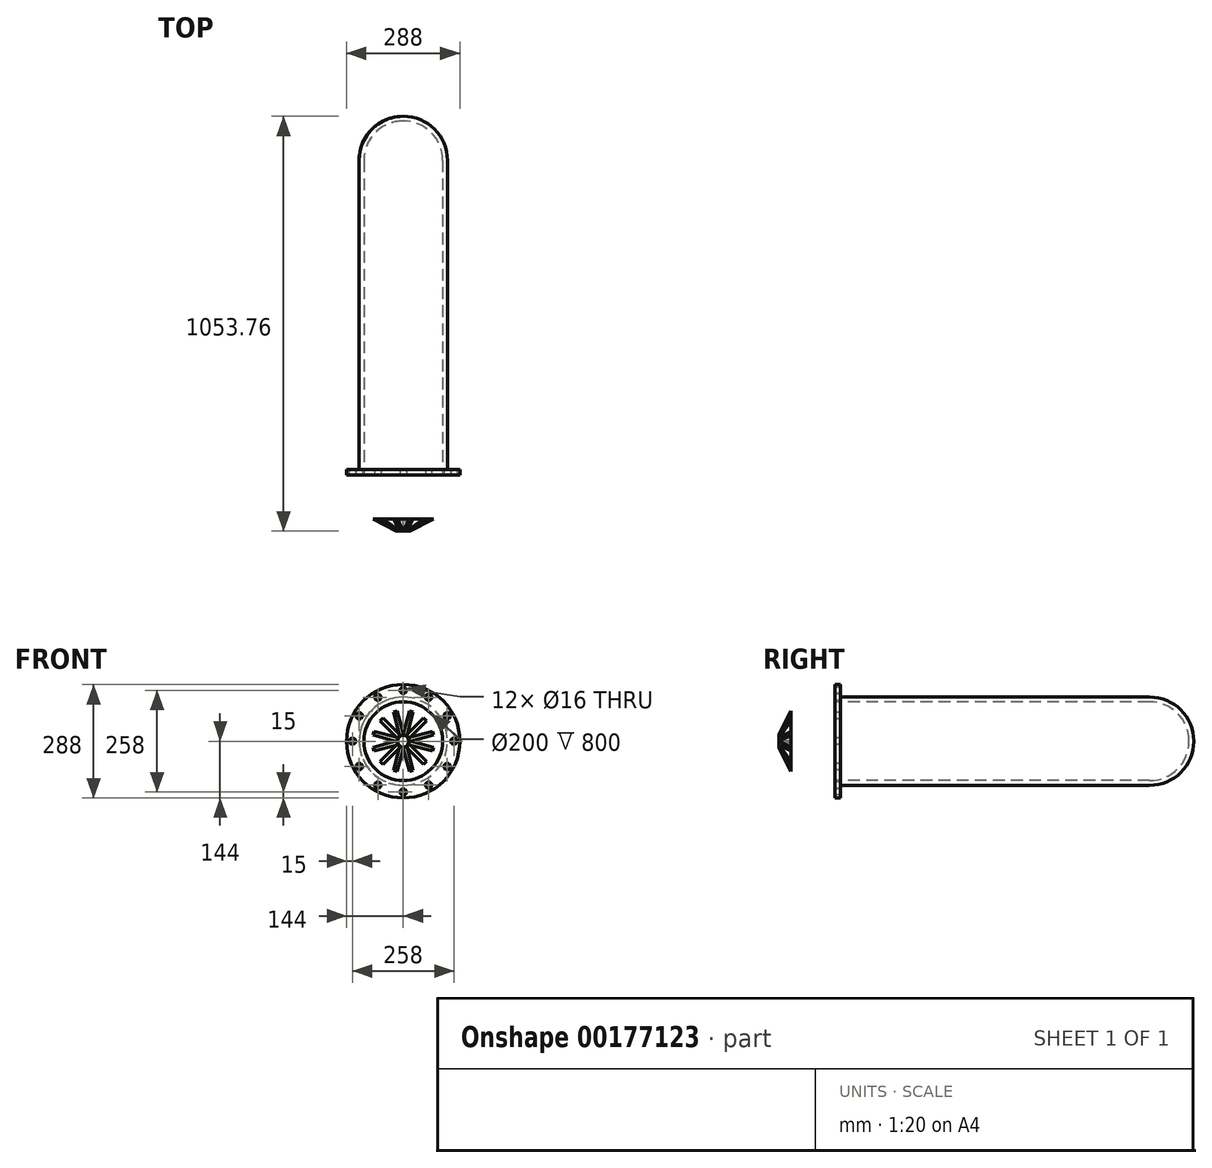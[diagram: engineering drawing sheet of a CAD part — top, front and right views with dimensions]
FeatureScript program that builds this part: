
annotation { "Feature Type Name" : "Feature", "Feature Type Description" : "" }
export const myFeature = defineFeature(function(context is Context, id is Id, definition is map)
    precondition{}
    {
        {
            var Q0;
            Q0=qCreatedBy(makeId("Top.planeOp"),FACE);
            var sketch = newSketch(context, id + "F0", { "sketchPlane" : qUnion([Q0])});
            skLineSegment(sketch, "E0", {"start": v(-144, 0) * mm, "end": v(-100, 0) * mm});
            skLineSegment(sketch, "E1", {"start": v(-100, 0) * mm, "end": v(-100, 800) * mm});
            skLineSegment(sketch, "E2", {"start": v(-144, 0) * mm, "end": v(-144, 14) * mm});
            skLineSegment(sketch, "E3", {"start": v(0, 912) * mm, "end": v(0, 900) * mm});
            skLineSegment(sketch, "E4", {"start": v(0, 0) * mm, "end": v(0, 900) * mm, "construction": true});
            skLineSegment(sketch, "E5", {"start": v(-144, 14) * mm, "end": v(-112, 14) * mm});
            skLineSegment(sketch, "E6", {"start": v(-112, 14) * mm, "end": v(-112, 800) * mm});
            skArc(sketch, "E7", {"start": v(0, 900) * mm, "mid": v(-70.71, 870.71) * mm, "end": v(-100, 800) * mm});
            skArc(sketch, "E8", {"start": v(0, 912) * mm, "mid": v(-79.2, 879.2) * mm, "end": v(-112, 800) * mm});
            skLineSegment(sketch, "E9", {"start": v(-112, 800) * mm, "end": v(0, 800) * mm, "construction": true});
            skSolve(sketch);
        }
        {
            var Q0;
            Q0 = qSketchRegion(id + "F0", true);
            var Q1;
            Q1=sQuery(id+"F0.wireOp",EDGE,"E4");
            revolve(context, id + "F1", {"entities" : qUnion([Q0]), "axis" : qUnion([Q1]), "revolveType" : RevolveType.FULL});
        }
        {
            var Q0;
            Q0=makeQuery(id+"F1.opRevolve","SWEPT_FACE",FACE,{"disambiguationData":[OSD([sQuery(id+"F0.wireOp",EDGE,"E0")])]});
            var sketch = newSketch(context, id + "F2", { "sketchPlane" : qUnion([Q0])});
            skCircle(sketch, "E10", {"center": v(0, 129) * mm, "radius": 8 * mm});
            skSolve(sketch);
        }
        {
            var Q0;
            Q0=makeQuery(id+"F2.imprint","IMPRINT",FACE,{"disambiguationData":[TD([[makeQuery(id+"F2.imprint","IMPRINT",EDGE,{"derivedFrom":sQuery(id+"F2.wireOp",EDGE,"E10")}),1.0]])]});
            extrude(context, id + "F3", {"entities" : qUnion([Q0]), "oppositeDirection" : true, "depth" : 20 * mm});
        }
        {
            var Q0;
            Q0=makeQuery(id+"F3.opExtrude","SWEPT_BODY",BODY,{"disambiguationData":[OSD([sQuery(id+"F2.wireOp",EDGE,"E10")])]});
            var Q1;
            Q1=makeQuery(id+"F1.opRevolve","SWEPT_EDGE",EDGE,{"disambiguationData":[OSD([sQuery(id+"F0.wireOp",EDGE,"E0"),sQuery(id+"F0.wireOp",EDGE,"E2")])]});
            circularPattern(context, id + "F4", {"entities" : qUnion([Q0]), "axis" : qUnion([Q1]), "angle" : 30 * degree, "instanceCount" : 12});
        }
        {
            var Q0;
            Q0=makeQuery(id+"F3.opExtrude","SWEPT_BODY",BODY,{"disambiguationData":[OSD([sQuery(id+"F2.wireOp",EDGE,"E10")])]});
            var Q1;
            Q1=makeQuery(id+"F4.opPattern","COPY",BODY,{"derivedFrom":makeQuery(id+"F3.opExtrude","SWEPT_BODY",BODY,{"disambiguationData":[OSD([sQuery(id+"F2.wireOp",EDGE,"E10")])]}),"instanceName":"1"});
            var Q2;
            Q2=makeQuery(id+"F4.opPattern","COPY",BODY,{"derivedFrom":makeQuery(id+"F3.opExtrude","SWEPT_BODY",BODY,{"disambiguationData":[OSD([sQuery(id+"F2.wireOp",EDGE,"E10")])]}),"instanceName":"4"});
            var Q3;
            Q3=makeQuery(id+"F4.opPattern","COPY",BODY,{"derivedFrom":makeQuery(id+"F3.opExtrude","SWEPT_BODY",BODY,{"disambiguationData":[OSD([sQuery(id+"F2.wireOp",EDGE,"E10")])]}),"instanceName":"3"});
            var Q4;
            Q4=makeQuery(id+"F4.opPattern","COPY",BODY,{"derivedFrom":makeQuery(id+"F3.opExtrude","SWEPT_BODY",BODY,{"disambiguationData":[OSD([sQuery(id+"F2.wireOp",EDGE,"E10")])]}),"instanceName":"2"});
            var Q5;
            Q5=makeQuery(id+"F4.opPattern","COPY",BODY,{"derivedFrom":makeQuery(id+"F3.opExtrude","SWEPT_BODY",BODY,{"disambiguationData":[OSD([sQuery(id+"F2.wireOp",EDGE,"E10")])]}),"instanceName":"9"});
            var Q6;
            Q6=makeQuery(id+"F4.opPattern","COPY",BODY,{"derivedFrom":makeQuery(id+"F3.opExtrude","SWEPT_BODY",BODY,{"disambiguationData":[OSD([sQuery(id+"F2.wireOp",EDGE,"E10")])]}),"instanceName":"10"});
            var Q7;
            Q7=makeQuery(id+"F4.opPattern","COPY",BODY,{"derivedFrom":makeQuery(id+"F3.opExtrude","SWEPT_BODY",BODY,{"disambiguationData":[OSD([sQuery(id+"F2.wireOp",EDGE,"E10")])]}),"instanceName":"11"});
            var Q8;
            Q8=makeQuery(id+"F4.opPattern","COPY",BODY,{"derivedFrom":makeQuery(id+"F3.opExtrude","SWEPT_BODY",BODY,{"disambiguationData":[OSD([sQuery(id+"F2.wireOp",EDGE,"E10")])]}),"instanceName":"8"});
            var Q9;
            Q9=makeQuery(id+"F4.opPattern","COPY",BODY,{"derivedFrom":makeQuery(id+"F3.opExtrude","SWEPT_BODY",BODY,{"disambiguationData":[OSD([sQuery(id+"F2.wireOp",EDGE,"E10")])]}),"instanceName":"7"});
            var Q10;
            Q10=makeQuery(id+"F4.opPattern","COPY",BODY,{"derivedFrom":makeQuery(id+"F3.opExtrude","SWEPT_BODY",BODY,{"disambiguationData":[OSD([sQuery(id+"F2.wireOp",EDGE,"E10")])]}),"instanceName":"6"});
            var Q11;
            Q11=makeQuery(id+"F4.opPattern","COPY",BODY,{"derivedFrom":makeQuery(id+"F3.opExtrude","SWEPT_BODY",BODY,{"disambiguationData":[OSD([sQuery(id+"F2.wireOp",EDGE,"E10")])]}),"instanceName":"5"});
            var Q12;
            Q12=makeQuery(id+"F1.opRevolve","SWEPT_BODY",BODY,{"disambiguationData":[OSD([sQuery(id+"F0.wireOp",EDGE,"E0"),sQuery(id+"F0.wireOp",EDGE,"E1"),sQuery(id+"F0.wireOp",EDGE,"E2"),sQuery(id+"F0.wireOp",EDGE,"E3"),sQuery(id+"F0.wireOp",EDGE,"E5"),sQuery(id+"F0.wireOp",EDGE,"E6"),sQuery(id+"F0.wireOp",EDGE,"E7"),sQuery(id+"F0.wireOp",EDGE,"E8")])]});
            booleanBodies(context, id + "F5", {"operationType" : BooleanOperationType.SUBTRACTION, "tools" : qUnion([Q0, Q1, Q2, Q3, Q4, Q5, Q6, Q7, Q8, Q9, Q10, Q11]), "targets" : qUnion([Q12])});
        }
        {
            var Q0;
            Q0=sQuery(id+"F0.wireOp",EDGE,"E4");
            cPlane(context, id + "F6", {"entities" : qUnion([Q0]), "cplaneType" : CPlaneType.LINE_ANGLE, "offset" : 25 * mm, "angle" : 45 * degree, "width" : 150 * mm, "height" : 150 * mm});
        }
        {
            var Q0;
            Q0=qCreatedBy(id+"F6.planeOp",FACE);
            var sketch = newSketch(context, id + "F7", { "sketchPlane" : qUnion([Q0])});
            skLineSegment(sketch, "E11", {"start": v(-111, 78) * mm, "end": v(-143, 14) * mm});
            skLineSegment(sketch, "E12", {"start": v(-143, 14) * mm, "end": v(-111, 14) * mm});
            skLineSegment(sketch, "E13", {"start": v(-111, 14) * mm, "end": v(-111, 78) * mm});
            skSolve(sketch);
        }
        {
            var Q0;
            Q0=makeQuery(id+"F7.imprint","IMPRINT",FACE,{"disambiguationData":[TD([[makeQuery(id+"F7.imprint","IMPRINT",EDGE,{"derivedFrom":sQuery(id+"F7.wireOp",EDGE,"E11")}),1.0]])]});
            extrude(context, id + "F8", {"entities" : qUnion([Q0]), "endBound" : BoundingType.SYMMETRIC, "depth" : 10 * mm});
        }
        {
            var Q0;
            Q0=makeQuery(id+"F8.opExtrude","SWEPT_BODY",BODY,{"disambiguationData":[OSD([sQuery(id+"F7.wireOp",EDGE,"E11"),sQuery(id+"F7.wireOp",EDGE,"E12"),sQuery(id+"F7.wireOp",EDGE,"E13")])]});
            var Q1;
            Q1=makeQuery(id+"F1.opRevolve","SWEPT_EDGE",EDGE,{"disambiguationData":[OSD([sQuery(id+"F0.wireOp",EDGE,"E2"),sQuery(id+"F0.wireOp",EDGE,"E5")])]});
            circularPattern(context, id + "F9", {"entities" : qUnion([Q0]), "axis" : qUnion([Q1]), "angle" : 30 * degree, "instanceCount" : 12});
        }
        {
            var Q0;
            Q0=makeQuery(id+"F1.opRevolve","SWEPT_FACE",FACE,{"disambiguationData":[OSD([sQuery(id+"F0.wireOp",EDGE,"E6")])]});
            fillet(context, id + "F10", {"entities" : qUnion([Q0]), "radius" : 2 * mm, "tangentPropagation" : true, "allowEdgeOverflow" : false});
        }
        {
            var Q0;
            Q0=makeQuery(id+"F9.opPattern","COPY",EDGE,{"derivedFrom":makeQuery(id+"F8.opExtrude","CAP_EDGE",EDGE,{"disambiguationData":[OSD([sQuery(id+"F7.wireOp",EDGE,"E12")])],"isStart":false}),"instanceName":"3"});
            var Q1;
            Q1=makeQuery(id+"F9.opPattern","COPY",EDGE,{"derivedFrom":makeQuery(id+"F8.opExtrude","SWEPT_EDGE",EDGE,{"disambiguationData":[OSD([sQuery(id+"F7.wireOp",EDGE,"E11"),sQuery(id+"F7.wireOp",EDGE,"E12")])]}),"instanceName":"3"});
            var Q2;
            Q2=makeQuery(id+"F9.opPattern","COPY",EDGE,{"derivedFrom":makeQuery(id+"F8.opExtrude","CAP_EDGE",EDGE,{"disambiguationData":[OSD([sQuery(id+"F7.wireOp",EDGE,"E12")])],"isStart":true}),"instanceName":"3"});
            var Q3;
            Q3=makeQuery(id+"F9.opPattern","COPY",EDGE,{"derivedFrom":makeQuery(id+"F8.opExtrude","CAP_EDGE",EDGE,{"disambiguationData":[OSD([sQuery(id+"F7.wireOp",EDGE,"E12")])],"isStart":false}),"instanceName":"4"});
            var Q4;
            Q4=makeQuery(id+"F9.opPattern","COPY",EDGE,{"derivedFrom":makeQuery(id+"F8.opExtrude","SWEPT_EDGE",EDGE,{"disambiguationData":[OSD([sQuery(id+"F7.wireOp",EDGE,"E11"),sQuery(id+"F7.wireOp",EDGE,"E12")])]}),"instanceName":"4"});
            var Q5;
            Q5=makeQuery(id+"F9.opPattern","COPY",EDGE,{"derivedFrom":makeQuery(id+"F8.opExtrude","CAP_EDGE",EDGE,{"disambiguationData":[OSD([sQuery(id+"F7.wireOp",EDGE,"E12")])],"isStart":true}),"instanceName":"4"});
            var Q6;
            Q6=makeQuery(id+"F9.opPattern","COPY",EDGE,{"derivedFrom":makeQuery(id+"F8.opExtrude","CAP_EDGE",EDGE,{"disambiguationData":[OSD([sQuery(id+"F7.wireOp",EDGE,"E12")])],"isStart":false}),"instanceName":"5"});
            var Q7;
            Q7=makeQuery(id+"F9.opPattern","COPY",EDGE,{"derivedFrom":makeQuery(id+"F8.opExtrude","SWEPT_EDGE",EDGE,{"disambiguationData":[OSD([sQuery(id+"F7.wireOp",EDGE,"E11"),sQuery(id+"F7.wireOp",EDGE,"E12")])]}),"instanceName":"5"});
            var Q8;
            Q8=makeQuery(id+"F9.opPattern","COPY",EDGE,{"derivedFrom":makeQuery(id+"F8.opExtrude","CAP_EDGE",EDGE,{"disambiguationData":[OSD([sQuery(id+"F7.wireOp",EDGE,"E12")])],"isStart":true}),"instanceName":"5"});
            var Q9;
            Q9=makeQuery(id+"F9.opPattern","COPY",EDGE,{"derivedFrom":makeQuery(id+"F8.opExtrude","CAP_EDGE",EDGE,{"disambiguationData":[OSD([sQuery(id+"F7.wireOp",EDGE,"E12")])],"isStart":false}),"instanceName":"6"});
            var Q10;
            Q10=makeQuery(id+"F9.opPattern","COPY",EDGE,{"derivedFrom":makeQuery(id+"F8.opExtrude","SWEPT_EDGE",EDGE,{"disambiguationData":[OSD([sQuery(id+"F7.wireOp",EDGE,"E11"),sQuery(id+"F7.wireOp",EDGE,"E12")])]}),"instanceName":"6"});
            var Q11;
            Q11=makeQuery(id+"F9.opPattern","COPY",EDGE,{"derivedFrom":makeQuery(id+"F8.opExtrude","CAP_EDGE",EDGE,{"disambiguationData":[OSD([sQuery(id+"F7.wireOp",EDGE,"E12")])],"isStart":true}),"instanceName":"6"});
            var Q12;
            Q12=makeQuery(id+"F9.opPattern","COPY",EDGE,{"derivedFrom":makeQuery(id+"F8.opExtrude","CAP_EDGE",EDGE,{"disambiguationData":[OSD([sQuery(id+"F7.wireOp",EDGE,"E12")])],"isStart":false}),"instanceName":"7"});
            var Q13;
            Q13=makeQuery(id+"F9.opPattern","COPY",EDGE,{"derivedFrom":makeQuery(id+"F8.opExtrude","SWEPT_EDGE",EDGE,{"disambiguationData":[OSD([sQuery(id+"F7.wireOp",EDGE,"E11"),sQuery(id+"F7.wireOp",EDGE,"E12")])]}),"instanceName":"7"});
            var Q14;
            Q14=makeQuery(id+"F9.opPattern","COPY",EDGE,{"derivedFrom":makeQuery(id+"F8.opExtrude","CAP_EDGE",EDGE,{"disambiguationData":[OSD([sQuery(id+"F7.wireOp",EDGE,"E12")])],"isStart":true}),"instanceName":"7"});
            var Q15;
            Q15=makeQuery(id+"F9.opPattern","COPY",EDGE,{"derivedFrom":makeQuery(id+"F8.opExtrude","CAP_EDGE",EDGE,{"disambiguationData":[OSD([sQuery(id+"F7.wireOp",EDGE,"E12")])],"isStart":false}),"instanceName":"8"});
            var Q16;
            Q16=makeQuery(id+"F9.opPattern","COPY",EDGE,{"derivedFrom":makeQuery(id+"F8.opExtrude","SWEPT_EDGE",EDGE,{"disambiguationData":[OSD([sQuery(id+"F7.wireOp",EDGE,"E11"),sQuery(id+"F7.wireOp",EDGE,"E12")])]}),"instanceName":"8"});
            var Q17;
            Q17=makeQuery(id+"F9.opPattern","COPY",EDGE,{"derivedFrom":makeQuery(id+"F8.opExtrude","CAP_EDGE",EDGE,{"disambiguationData":[OSD([sQuery(id+"F7.wireOp",EDGE,"E12")])],"isStart":true}),"instanceName":"8"});
            var Q18;
            Q18=makeQuery(id+"F9.opPattern","COPY",EDGE,{"derivedFrom":makeQuery(id+"F8.opExtrude","CAP_EDGE",EDGE,{"disambiguationData":[OSD([sQuery(id+"F7.wireOp",EDGE,"E12")])],"isStart":false}),"instanceName":"9"});
            var Q19;
            Q19=makeQuery(id+"F9.opPattern","COPY",EDGE,{"derivedFrom":makeQuery(id+"F8.opExtrude","SWEPT_EDGE",EDGE,{"disambiguationData":[OSD([sQuery(id+"F7.wireOp",EDGE,"E11"),sQuery(id+"F7.wireOp",EDGE,"E12")])]}),"instanceName":"9"});
            var Q20;
            Q20=makeQuery(id+"F9.opPattern","COPY",EDGE,{"derivedFrom":makeQuery(id+"F8.opExtrude","CAP_EDGE",EDGE,{"disambiguationData":[OSD([sQuery(id+"F7.wireOp",EDGE,"E12")])],"isStart":true}),"instanceName":"9"});
            var Q21;
            Q21=makeQuery(id+"F9.opPattern","COPY",EDGE,{"derivedFrom":makeQuery(id+"F8.opExtrude","CAP_EDGE",EDGE,{"disambiguationData":[OSD([sQuery(id+"F7.wireOp",EDGE,"E12")])],"isStart":false}),"instanceName":"10"});
            var Q22;
            Q22=makeQuery(id+"F9.opPattern","COPY",EDGE,{"derivedFrom":makeQuery(id+"F8.opExtrude","SWEPT_EDGE",EDGE,{"disambiguationData":[OSD([sQuery(id+"F7.wireOp",EDGE,"E11"),sQuery(id+"F7.wireOp",EDGE,"E12")])]}),"instanceName":"10"});
            var Q23;
            Q23=makeQuery(id+"F9.opPattern","COPY",EDGE,{"derivedFrom":makeQuery(id+"F8.opExtrude","CAP_EDGE",EDGE,{"disambiguationData":[OSD([sQuery(id+"F7.wireOp",EDGE,"E12")])],"isStart":true}),"instanceName":"10"});
            var Q24;
            Q24=makeQuery(id+"F9.opPattern","COPY",EDGE,{"derivedFrom":makeQuery(id+"F8.opExtrude","CAP_EDGE",EDGE,{"disambiguationData":[OSD([sQuery(id+"F7.wireOp",EDGE,"E12")])],"isStart":false}),"instanceName":"11"});
            var Q25;
            Q25=makeQuery(id+"F9.opPattern","COPY",EDGE,{"derivedFrom":makeQuery(id+"F8.opExtrude","SWEPT_EDGE",EDGE,{"disambiguationData":[OSD([sQuery(id+"F7.wireOp",EDGE,"E11"),sQuery(id+"F7.wireOp",EDGE,"E12")])]}),"instanceName":"11"});
            var Q26;
            Q26=makeQuery(id+"F9.opPattern","COPY",EDGE,{"derivedFrom":makeQuery(id+"F8.opExtrude","CAP_EDGE",EDGE,{"disambiguationData":[OSD([sQuery(id+"F7.wireOp",EDGE,"E12")])],"isStart":true}),"instanceName":"11"});
            var Q27;
            Q27=makeQuery(id+"F8.opExtrude","CAP_EDGE",EDGE,{"disambiguationData":[OSD([sQuery(id+"F7.wireOp",EDGE,"E12")])],"isStart":false});
            var Q28;
            Q28=makeQuery(id+"F8.opExtrude","SWEPT_EDGE",EDGE,{"disambiguationData":[OSD([sQuery(id+"F7.wireOp",EDGE,"E11"),sQuery(id+"F7.wireOp",EDGE,"E12")])]});
            var Q29;
            Q29=makeQuery(id+"F8.opExtrude","CAP_EDGE",EDGE,{"disambiguationData":[OSD([sQuery(id+"F7.wireOp",EDGE,"E12")])],"isStart":true});
            var Q30;
            Q30=makeQuery(id+"F9.opPattern","COPY",EDGE,{"derivedFrom":makeQuery(id+"F8.opExtrude","CAP_EDGE",EDGE,{"disambiguationData":[OSD([sQuery(id+"F7.wireOp",EDGE,"E12")])],"isStart":false}),"instanceName":"1"});
            var Q31;
            Q31=makeQuery(id+"F9.opPattern","COPY",EDGE,{"derivedFrom":makeQuery(id+"F8.opExtrude","SWEPT_EDGE",EDGE,{"disambiguationData":[OSD([sQuery(id+"F7.wireOp",EDGE,"E11"),sQuery(id+"F7.wireOp",EDGE,"E12")])]}),"instanceName":"1"});
            var Q32;
            Q32=makeQuery(id+"F9.opPattern","COPY",EDGE,{"derivedFrom":makeQuery(id+"F8.opExtrude","CAP_EDGE",EDGE,{"disambiguationData":[OSD([sQuery(id+"F7.wireOp",EDGE,"E12")])],"isStart":true}),"instanceName":"1"});
            var Q33;
            Q33=makeQuery(id+"F9.opPattern","COPY",EDGE,{"derivedFrom":makeQuery(id+"F8.opExtrude","CAP_EDGE",EDGE,{"disambiguationData":[OSD([sQuery(id+"F7.wireOp",EDGE,"E12")])],"isStart":false}),"instanceName":"2"});
            var Q34;
            Q34=makeQuery(id+"F9.opPattern","COPY",EDGE,{"derivedFrom":makeQuery(id+"F8.opExtrude","SWEPT_EDGE",EDGE,{"disambiguationData":[OSD([sQuery(id+"F7.wireOp",EDGE,"E11"),sQuery(id+"F7.wireOp",EDGE,"E12")])]}),"instanceName":"2"});
            var Q35;
            Q35=makeQuery(id+"F9.opPattern","COPY",EDGE,{"derivedFrom":makeQuery(id+"F8.opExtrude","CAP_EDGE",EDGE,{"disambiguationData":[OSD([sQuery(id+"F7.wireOp",EDGE,"E12")])],"isStart":true}),"instanceName":"2"});
            fillet(context, id + "F11", {"entities" : qUnion([Q0, Q1, Q2, Q3, Q4, Q5, Q6, Q7, Q8, Q9, Q10, Q11, Q12, Q13, Q14, Q15, Q16, Q17, Q18, Q19, Q20, Q21, Q22, Q23, Q24, Q25, Q26, Q27, Q28, Q29, Q30, Q31, Q32, Q33, Q34, Q35]), "radius" : 2 * mm, "tangentPropagation" : true, "allowEdgeOverflow" : false});
        }
    });
